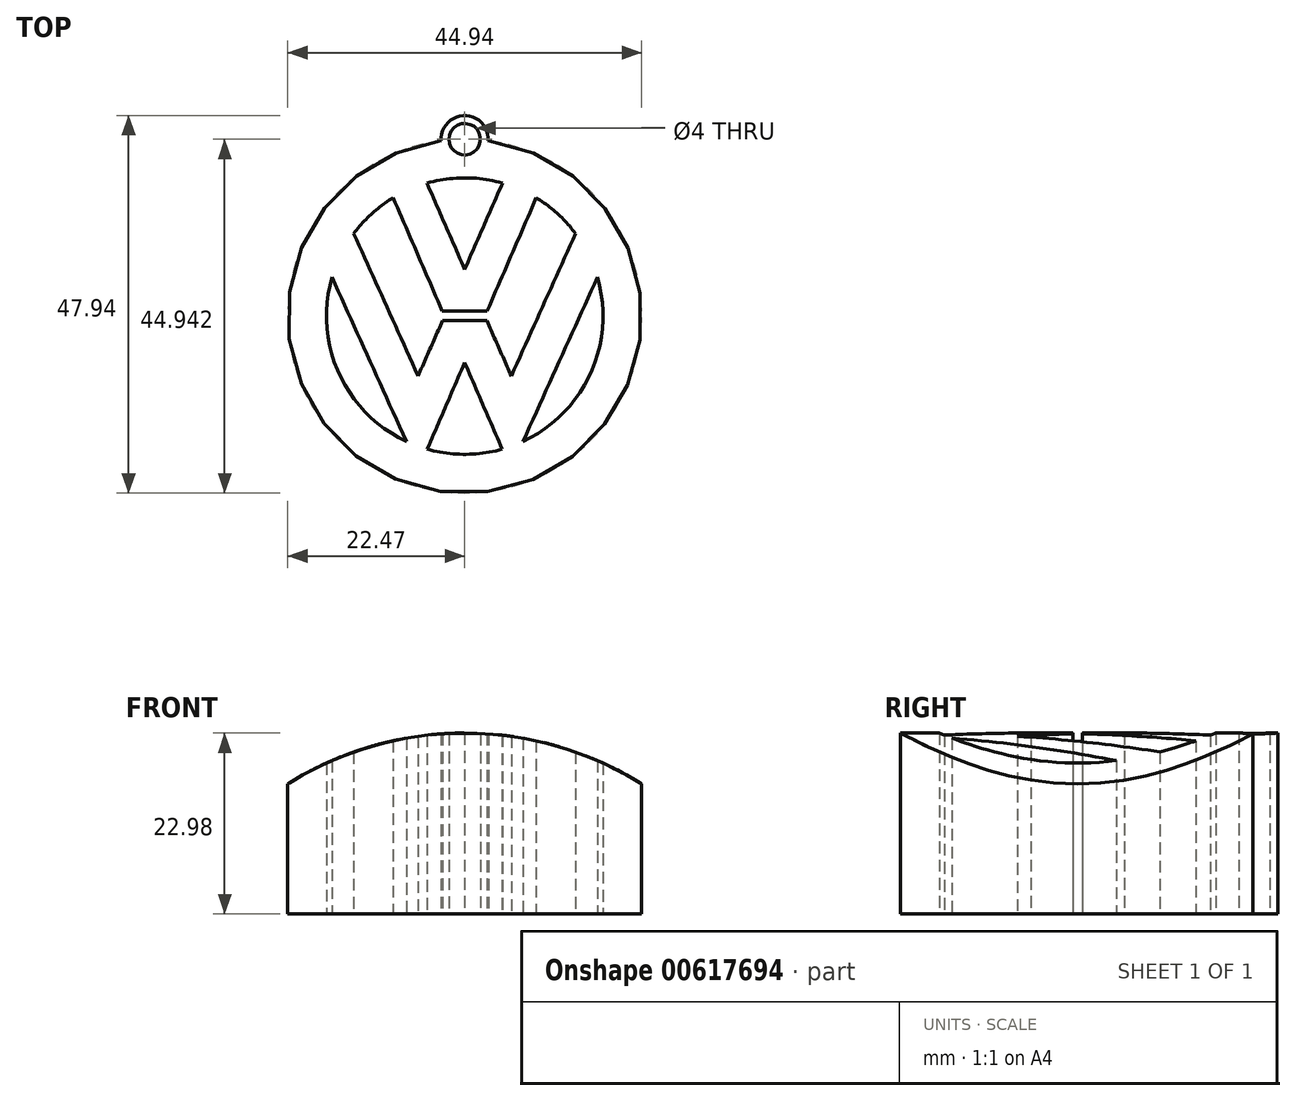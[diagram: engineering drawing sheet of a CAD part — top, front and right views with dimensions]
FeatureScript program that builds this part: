
annotation { "Feature Type Name" : "Feature", "Feature Type Description" : "" }
export const myFeature = defineFeature(function(context is Context, id is Id, definition is map)
    precondition{}
    {
        {
            var Q0;
            Q0=qCreatedBy(makeId("Top.planeOp"),FACE);
            var sketch = newSketch(context, id + "F0", { "sketchPlane" : qUnion([Q0])});
            skArc(sketch, "E0", {"start": v(-16.85, 4.93) * mm, "mid": v(-16, -7.24) * mm, "end": v(-7.41, -15.92) * mm});
            skLineSegment(sketch, "E1", {"start": v(-4.8, 16.9) * mm, "end": v(0, 5.94) * mm});
            skLineSegment(sketch, "E2", {"start": v(-9.09, 15.03) * mm, "end": v(-2.85, 0.64) * mm});
            skLineSegment(sketch, "E3", {"start": v(-2.85, 0.64) * mm, "end": v(0, 0.64) * mm});
            skLineSegment(sketch, "E4", {"start": v(0, -0.58) * mm, "end": v(-2.8, -0.58) * mm});
            skLineSegment(sketch, "E5", {"start": v(-2.8, -0.58) * mm, "end": v(-5.92, -7.6) * mm});
            skLineSegment(sketch, "E6", {"start": v(-5.92, -7.6) * mm, "end": v(-14.09, 10.48) * mm});
            skLineSegment(sketch, "E7", {"start": v(-16.85, 4.93) * mm, "end": v(-7.41, -15.92) * mm});
            skLineSegment(sketch, "E8", {"start": v(0, -5.9) * mm, "end": v(-4.77, -16.9) * mm});
            skArc(sketch, "E9.trimOffspring", {"start": v(-9.09, 15.03) * mm, "mid": v(-11.8, 13) * mm, "end": v(-14.09, 10.48) * mm});
            skArc(sketch, "E10.trimOffspring", {"start": v(0, 17.56) * mm, "mid": v(-2.42, 17.4) * mm, "end": v(-4.8, 16.9) * mm});
            skArc(sketch, "E11.trimOffspring", {"start": v(-4.77, -16.9) * mm, "mid": v(-2.4, -17.4) * mm, "end": v(0, -17.56) * mm});
            skLineSegment(sketch, "E12.MirrorCS", {"start": v(2.8, -0.58) * mm, "end": v(5.92, -7.6) * mm});
            skLineSegment(sketch, "E13.MirrorCS", {"start": v(0, -0.58) * mm, "end": v(2.8, -0.58) * mm});
            skLineSegment(sketch, "E14.MirrorCS", {"start": v(2.85, 0.64) * mm, "end": v(0, 0.64) * mm});
            skArc(sketch, "E15.MirrorCS", {"start": v(0, 17.56) * mm, "mid": v(2.42, 17.4) * mm, "end": v(4.8, 16.9) * mm});
            skLineSegment(sketch, "E16.MirrorCS", {"start": v(5.92, -7.6) * mm, "end": v(14.09, 10.48) * mm});
            skLineSegment(sketch, "E17.MirrorCS", {"start": v(4.8, 16.9) * mm, "end": v(0, 5.94) * mm});
            skArc(sketch, "E18.MirrorCS", {"start": v(9.09, 15.03) * mm, "mid": v(11.8, 13) * mm, "end": v(14.09, 10.48) * mm});
            skArc(sketch, "E19.MirrorCS", {"start": v(4.77, -16.9) * mm, "mid": v(2.4, -17.4) * mm, "end": v(0, -17.56) * mm});
            skArc(sketch, "E20.MirrorCS", {"start": v(16.85, 4.93) * mm, "mid": v(16, -7.24) * mm, "end": v(7.41, -15.92) * mm});
            skLineSegment(sketch, "E21.MirrorCS", {"start": v(9.09, 15.03) * mm, "end": v(2.85, 0.64) * mm});
            skLineSegment(sketch, "E22.MirrorCS", {"start": v(16.85, 4.93) * mm, "end": v(7.41, -15.92) * mm});
            skLineSegment(sketch, "E23.MirrorCS", {"start": v(0, -5.9) * mm, "end": v(4.77, -16.9) * mm});
            skArc(sketch, "E24", {"start": v(-3, 22.27) * mm, "mid": v(0, -22.47) * mm, "end": v(3, 22.27) * mm});
            skArc(sketch, "E25", {"start": v(3, 22.27) * mm, "mid": v(0, 25.47) * mm, "end": v(-3, 22.27) * mm});
            skCircle(sketch, "E26", {"center": v(0, 22.47) * mm, "radius": 2 * mm});
            skSolve(sketch);
        }
        {
            var Q0;
            Q0 = qSketchRegion(id + "F0", true);
            extrude(context, id + "F1", {"entities" : qUnion([Q0]), "depth" : 25 * mm, "offsetDistance" : 25 * mm});
        }
        {
            var Q0;
            Q0=qCreatedBy(makeId("Front.planeOp"),FACE);
            var sketch = newSketch(context, id + "F2", { "sketchPlane" : qUnion([Q0])});
            skArc(sketch, "E27", {"start": v(25, 14.8) * mm, "mid": v(0, 22.98) * mm, "end": v(-25, 14.8) * mm});
            skLineSegment(sketch, "E28", {"start": v(-25, 14.8) * mm, "end": v(-25, 26.38) * mm});
            skLineSegment(sketch, "E29", {"start": v(-25, 26.38) * mm, "end": v(25.06, 26.38) * mm});
            skLineSegment(sketch, "E30", {"start": v(25.06, 26.38) * mm, "end": v(25, 14.8) * mm});
            skSolve(sketch);
        }
        {
            var Q0;
            Q0 = qSketchRegion(id + "F2", true);
            extrude(context, id + "F3", {"entities" : qUnion([Q0]), "operationType" : NewBodyOperationType.REMOVE, "endBound" : BoundingType.SYMMETRIC, "oppositeDirection" : true, "depth" : 59 * mm, "offsetDistance" : 25 * mm});
        }
    });
